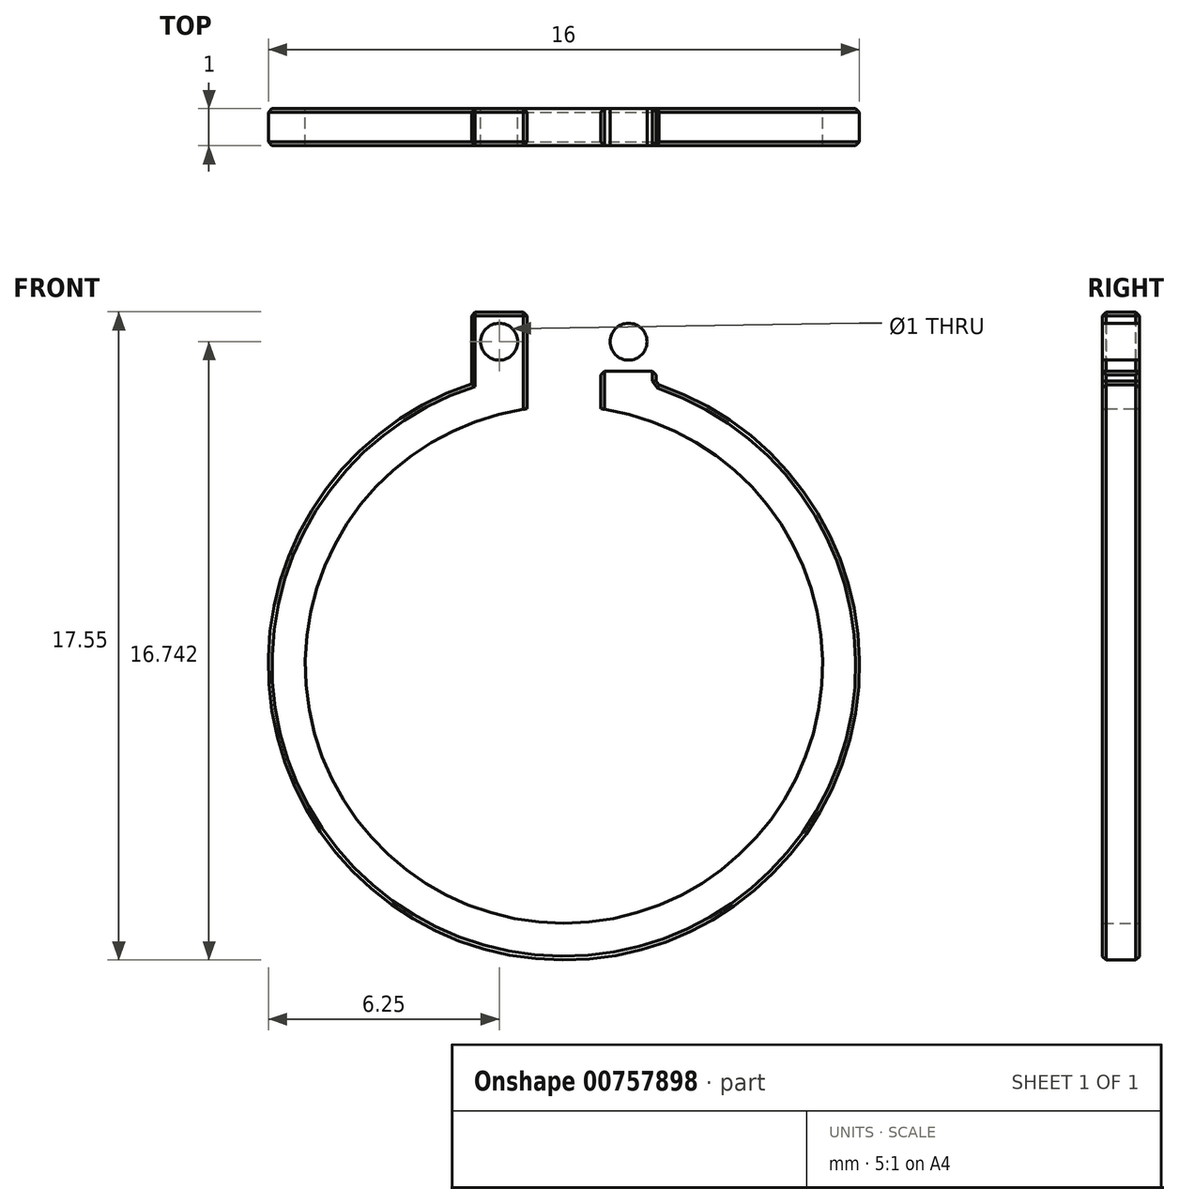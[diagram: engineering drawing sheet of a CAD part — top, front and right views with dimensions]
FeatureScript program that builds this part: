
annotation { "Feature Type Name" : "Feature", "Feature Type Description" : "" }
export const myFeature = defineFeature(function(context is Context, id is Id, definition is map)
    precondition{}
    {
        {
            var Q0;
            Q0=qCreatedBy(makeId("Front.planeOp"),FACE);
            var sketch = newSketch(context, id + "F0", { "sketchPlane" : qUnion([Q0])});
            skCircle(sketch, "E0", {"center": v(0, 0) * mm, "radius": 8 * mm});
            skCircle(sketch, "E1", {"center": v(0, 0) * mm, "radius": 7 * mm});
            skLineSegment(sketch, "E2", {"start": v(-1, 7.94) * mm, "end": v(-1, 6.93) * mm});
            skLineSegment(sketch, "E3", {"start": v(1, 7.94) * mm, "end": v(1, 6.93) * mm});
            skLineSegment(sketch, "E4", {"start": v(-2.5, 6.54) * mm, "end": v(-2.5, 9.55) * mm});
            skLineSegment(sketch, "E5.MirrorCS", {"start": v(2.5, 6.54) * mm, "end": v(2.5, 9.55) * mm});
            skLineSegment(sketch, "E6", {"start": v(-1, 7.94) * mm, "end": v(-1, 9.55) * mm});
            skLineSegment(sketch, "E7", {"start": v(-1, 9.55) * mm, "end": v(-2.5, 9.55) * mm});
            skLineSegment(sketch, "E8", {"start": v(-1.75, 9.55) * mm, "end": v(-1.75, 6.85) * mm, "construction": true});
            skLineSegment(sketch, "E9", {"start": v(-1, 8.74) * mm, "end": v(-2.5, 8.74) * mm, "construction": true});
            skCircle(sketch, "E10", {"center": v(-1.75, 8.74) * mm, "radius": 0.5 * mm});
            skLineSegment(sketch, "E11.MirrorCS", {"start": v(-1, 7.94) * mm, "end": v(-2.5, 7.94) * mm});
            skLineSegment(sketch, "E12.MirrorCS", {"start": v(-1, 9.55) * mm, "end": v(-1, 7.94) * mm});
            skLineSegment(sketch, "E13.MirrorCS", {"start": v(-1.75, 7.94) * mm, "end": v(-1.75, 10.63) * mm, "construction": true});
            skCircle(sketch, "E14.MirrorC", {"center": v(1.75, 8.74) * mm, "radius": 0.5 * mm});
            skLineSegment(sketch, "E15.MirrorCS", {"start": v(1, 9.55) * mm, "end": v(2.5, 9.55) * mm});
            skLineSegment(sketch, "E16.MirrorCS", {"start": v(1, 8.74) * mm, "end": v(2.5, 8.74) * mm, "construction": true});
            skLineSegment(sketch, "E17.MirrorCS", {"start": v(1.75, 7.94) * mm, "end": v(1.75, 10.63) * mm, "construction": true});
            skLineSegment(sketch, "E18.MirrorCS", {"start": v(1, 7.94) * mm, "end": v(2.5, 7.94) * mm});
            skLineSegment(sketch, "E19.MirrorCS", {"start": v(1, 7.94) * mm, "end": v(1, 9.55) * mm});
            skSolve(sketch);
        }
        {
            var Q0;
            {var subQ0=sQuery(id+"F0.wireOp",EDGE,"E18.MirrorCS");Q0=makeQuery(id+"F0.imprint","IMPRINT",FACE,{"disambiguationData":[TD([[makeQuery(id+"F0.imprint","IMPRINT",EDGE,{"derivedFrom":subQ0}),-1.0]])]});}
            var Q1;
            {var subQ0=sQuery(id+"F0.wireOp",EDGE,"E11.MirrorCS");Q1=makeQuery(id+"F0.imprint","IMPRINT",FACE,{"disambiguationData":[TD([[makeQuery(id+"F0.imprint","IMPRINT",EDGE,{"derivedFrom":subQ0}),1.0]])]});}
            var Q2;
            {var subQ0=sQuery(id+"F0.wireOp",EDGE,"E7");Q2=makeQuery(id+"F0.imprint","IMPRINT",FACE,{"disambiguationData":[TD([[makeQuery(id+"F0.imprint","IMPRINT",EDGE,{"derivedFrom":subQ0}),1.0]])]});}
            var Q3;
            Q3=makeQuery(id+"F0.imprint","IMPRINT",FACE,{"disambiguationData":[TD([[makeQuery(id+"F0.imprint","IMPRINT",EDGE,{"derivedFrom":sQuery(id+"F0.wireOp",EDGE,"E14.MirrorC")}),1.0]])]});
            var Q4;
            {var subQ0=sQuery(id+"F0.wireOp",EDGE,"E5.MirrorCS");var subQ1=sQuery(id+"F0.wireOp",EDGE,"E0");var subQ2=makeQuery(id+"F0.imprint","INTERSECT",VERTEX,{"derivedFrom":[subQ1,subQ0]});Q4=makeQuery(id+"F0.imprint","IMPRINT",FACE,{"disambiguationData":[TD([[makeQuery(id+"F0.imprint","IMPRINT",EDGE,{"disambiguationData":[TD([[subQ2,1.0]])],"derivedFrom":subQ1}),1.0]])]});}
            var Q5;
            {var subQ0=sQuery(id+"F0.wireOp",EDGE,"E3");Q5=makeQuery(id+"F0.imprint","IMPRINT",FACE,{"disambiguationData":[TD([[makeQuery(id+"F0.imprint","IMPRINT",EDGE,{"derivedFrom":subQ0}),1.0]])]});}
            var Q6;
            {var subQ0=sQuery(id+"F0.wireOp",EDGE,"E2");Q6=makeQuery(id+"F0.imprint","IMPRINT",FACE,{"disambiguationData":[TD([[makeQuery(id+"F0.imprint","IMPRINT",EDGE,{"derivedFrom":subQ0}),-1.0]])]});}
            extrude(context, id + "F1", {"entities" : qUnion([Q0, Q1, Q2, Q3, Q4, Q5, Q6]), "depth" : 1 * mm, "offsetDistance" : 25 * mm});
        }
        {
            var Q0;
            Q0=makeQuery(id+"F1.opExtrude","CAP_EDGE",EDGE,{"disambiguationData":[OSD([sQuery(id+"F0.wireOp",EDGE,"E7")])],"isStart":false});
            var Q1;
            Q1=makeQuery(id+"F1.opExtrude","CAP_EDGE",EDGE,{"disambiguationData":[OSD([sQuery(id+"F0.wireOp",EDGE,"E2"),sQuery(id+"F0.wireOp",EDGE,"E12.MirrorCS")])],"isStart":false});
            var Q2;
            Q2=makeQuery(id+"F1.opExtrude","CAP_EDGE",EDGE,{"disambiguationData":[OSD([sQuery(id+"F0.wireOp",EDGE,"E4")])],"isStart":false});
            var Q3;
            Q3=makeQuery(id+"F1.opExtrude","CAP_EDGE",EDGE,{"disambiguationData":[OSD([sQuery(id+"F0.wireOp",EDGE,"E0")])],"isStart":false});
            var Q4;
            Q4=makeQuery(id+"F1.opExtrude","CAP_EDGE",EDGE,{"disambiguationData":[OSD([sQuery(id+"F0.wireOp",EDGE,"E5.MirrorCS")])],"isStart":false});
            var Q5;
            Q5=makeQuery(id+"F1.opExtrude","CAP_EDGE",EDGE,{"disambiguationData":[OSD([sQuery(id+"F0.wireOp",EDGE,"E15.MirrorCS")])],"isStart":false});
            var Q6;
            Q6=makeQuery(id+"F1.opExtrude","CAP_EDGE",EDGE,{"disambiguationData":[OSD([sQuery(id+"F0.wireOp",EDGE,"E3"),sQuery(id+"F0.wireOp",EDGE,"E19.MirrorCS")])],"isStart":false});
            var Q7;
            Q7=makeQuery(id+"F1.opExtrude","CAP_EDGE",EDGE,{"disambiguationData":[OSD([sQuery(id+"F0.wireOp",EDGE,"E15.MirrorCS")])],"isStart":true});
            var Q8;
            Q8=makeQuery(id+"F1.opExtrude","SWEPT_EDGE",EDGE,{"disambiguationData":[OSD([sQuery(id+"F0.wireOp",EDGE,"E15.MirrorCS"),sQuery(id+"F0.wireOp",EDGE,"E19.MirrorCS")])]});
            var Q9;
            Q9=makeQuery(id+"F1.opExtrude","SWEPT_EDGE",EDGE,{"disambiguationData":[OSD([sQuery(id+"F0.wireOp",EDGE,"E5.MirrorCS"),sQuery(id+"F0.wireOp",EDGE,"E15.MirrorCS")])]});
            var Q10;
            Q10=makeQuery(id+"F1.opExtrude","SWEPT_EDGE",EDGE,{"disambiguationData":[OSD([sQuery(id+"F0.wireOp",EDGE,"E7"),sQuery(id+"F0.wireOp",EDGE,"E12.MirrorCS")])]});
            var Q11;
            Q11=makeQuery(id+"F1.opExtrude","CAP_EDGE",EDGE,{"disambiguationData":[OSD([sQuery(id+"F0.wireOp",EDGE,"E7")])],"isStart":true});
            var Q12;
            Q12=makeQuery(id+"F1.opExtrude","SWEPT_EDGE",EDGE,{"disambiguationData":[OSD([sQuery(id+"F0.wireOp",EDGE,"E4"),sQuery(id+"F0.wireOp",EDGE,"E7")])]});
            var Q13;
            Q13=makeQuery(id+"F1.opExtrude","CAP_EDGE",EDGE,{"disambiguationData":[OSD([sQuery(id+"F0.wireOp",EDGE,"E2"),sQuery(id+"F0.wireOp",EDGE,"E12.MirrorCS")])],"isStart":true});
            var Q14;
            Q14=makeQuery(id+"F1.opExtrude","CAP_EDGE",EDGE,{"disambiguationData":[OSD([sQuery(id+"F0.wireOp",EDGE,"E3"),sQuery(id+"F0.wireOp",EDGE,"E19.MirrorCS")])],"isStart":true});
            var Q15;
            Q15=makeQuery(id+"F1.opExtrude","CAP_EDGE",EDGE,{"disambiguationData":[OSD([sQuery(id+"F0.wireOp",EDGE,"E5.MirrorCS")])],"isStart":true});
            var Q16;
            Q16=makeQuery(id+"F1.opExtrude","CAP_EDGE",EDGE,{"disambiguationData":[OSD([sQuery(id+"F0.wireOp",EDGE,"E4")])],"isStart":true});
            var Q17;
            Q17=makeQuery(id+"F1.opExtrude","CAP_EDGE",EDGE,{"disambiguationData":[OSD([sQuery(id+"F0.wireOp",EDGE,"E0")])],"isStart":true});
            chamfer(context, id + "F2", {"entities" : qUnion([Q0, Q1, Q2, Q3, Q4, Q5, Q6, Q7, Q8, Q9, Q10, Q11, Q12, Q13, Q14, Q15, Q16, Q17]), "width" : .1 * mm, "tangentPropagation" : true});
        }
    });
